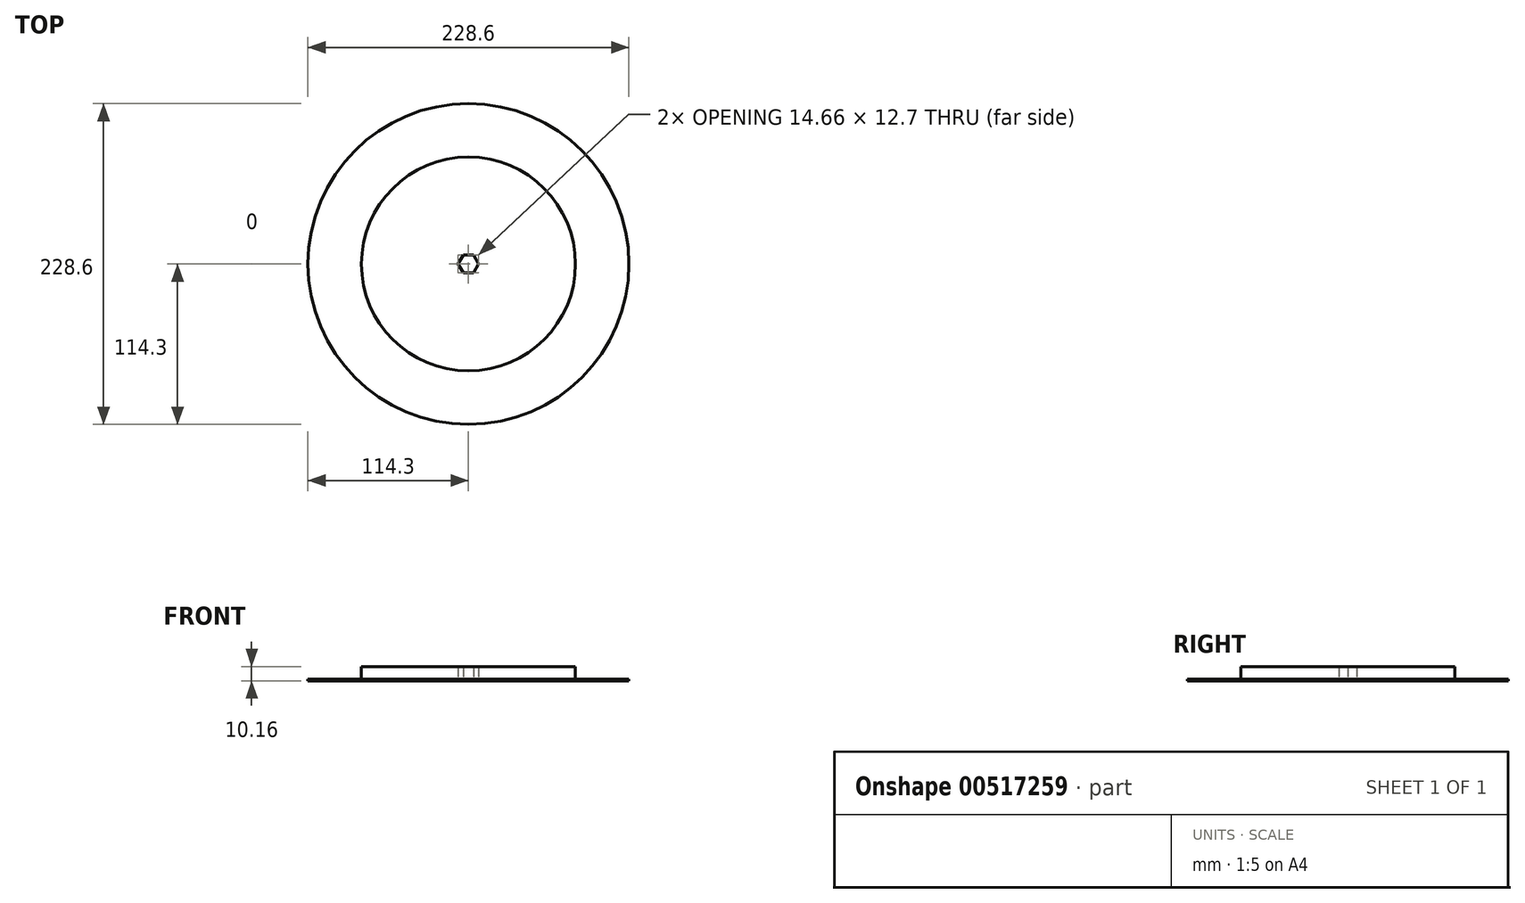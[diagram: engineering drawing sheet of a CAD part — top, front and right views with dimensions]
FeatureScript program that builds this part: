
annotation { "Feature Type Name" : "Feature", "Feature Type Description" : "" }
export const myFeature = defineFeature(function(context is Context, id is Id, definition is map)
    precondition{}
    {
        {
            var Q0;
            Q0=qCreatedBy(makeId("Top.planeOp"),FACE);
            var sketch = newSketch(context, id + "F0", { "sketchPlane" : qUnion([Q0])});
            skCircle(sketch, "E0", {"center": v(0, 0) * mm, "radius": 114.3 * mm});
            skSolve(sketch);
        }
        {
            var Q0;
            Q0=qCreatedBy(makeId("Top.planeOp"),FACE);
            var sketch = newSketch(context, id + "F1", { "sketchPlane" : qUnion([Q0])});
            skCircle(sketch, "E1", {"center": v(0, 0) * mm, "radius": 76.2 * mm});
            skSolve(sketch);
        }
        {
            var Q0;
            Q0=makeQuery(id+"F0.imprint","IMPRINT",FACE,{"disambiguationData":[TD([[makeQuery(id+"F0.imprint","IMPRINT",EDGE,{"derivedFrom":sQuery(id+"F0.wireOp",EDGE,"E0")}),1.0]])]});
            var Q1;
            Q1=sQuery(id+"F1.wireOp",EDGE,"E1");
            extrude(context, id + "F2", {"entities" : qUnion([Q0]), "surfaceEntities" : qUnion([Q1]), "depth" : 1.02 * mm, "offsetDistance" : 25.4 * mm});
        }
        {
            var Q0;
            Q0=makeQuery(id+"F1.imprint","IMPRINT",FACE,{"disambiguationData":[TD([[makeQuery(id+"F1.imprint","IMPRINT",EDGE,{"derivedFrom":sQuery(id+"F1.wireOp",EDGE,"E1")}),1.0]])]});
            var Q1;
            Q1=sQuery(id+"F0.wireOp",EDGE,"E0");
            extrude(context, id + "F3", {"entities" : qUnion([Q0]), "surfaceEntities" : qUnion([Q1]), "depth" : 10.16 * mm, "offsetDistance" : 25.4 * mm});
        }
        {
            var Q0;
            Q0=qCreatedBy(makeId("Top.planeOp"),FACE);
            var sketch = newSketch(context, id + "F4", { "sketchPlane" : qUnion([Q0])});
            skCircle(sketch, "E2.cCircle", {"center": v(0, 0) * mm, "radius": 6.35 * mm, "construction": true});
            skLineSegment(sketch, "E2.0", {"start": v(3.67, 6.35) * mm, "end": v(7.33, 0) * mm});
            skLineSegment(sketch, "E2.1", {"start": v(7.33, 0) * mm, "end": v(3.67, -6.35) * mm});
            skLineSegment(sketch, "E2.2", {"start": v(3.67, -6.35) * mm, "end": v(-3.67, -6.35) * mm});
            skLineSegment(sketch, "E2.3", {"start": v(-3.67, -6.35) * mm, "end": v(-7.33, 0) * mm});
            skLineSegment(sketch, "E2.4", {"start": v(-7.33, 0) * mm, "end": v(-3.67, 6.35) * mm});
            skLineSegment(sketch, "E2.5", {"start": v(-3.67, 6.35) * mm, "end": v(3.67, 6.35) * mm});
            skPoint(sketch, "E2.0.midPoint", {"position": v(5.5, 3.17) * mm});
            skSolve(sketch);
        }
        {
            var Q0;
            Q0 = qSketchRegion(id + "F4", true);
            extrude(context, id + "F5", {"entities" : qUnion([Q0]), "operationType" : NewBodyOperationType.REMOVE, "depth" : 25.4 * mm, "offsetDistance" : 25.4 * mm});
        }
    });
